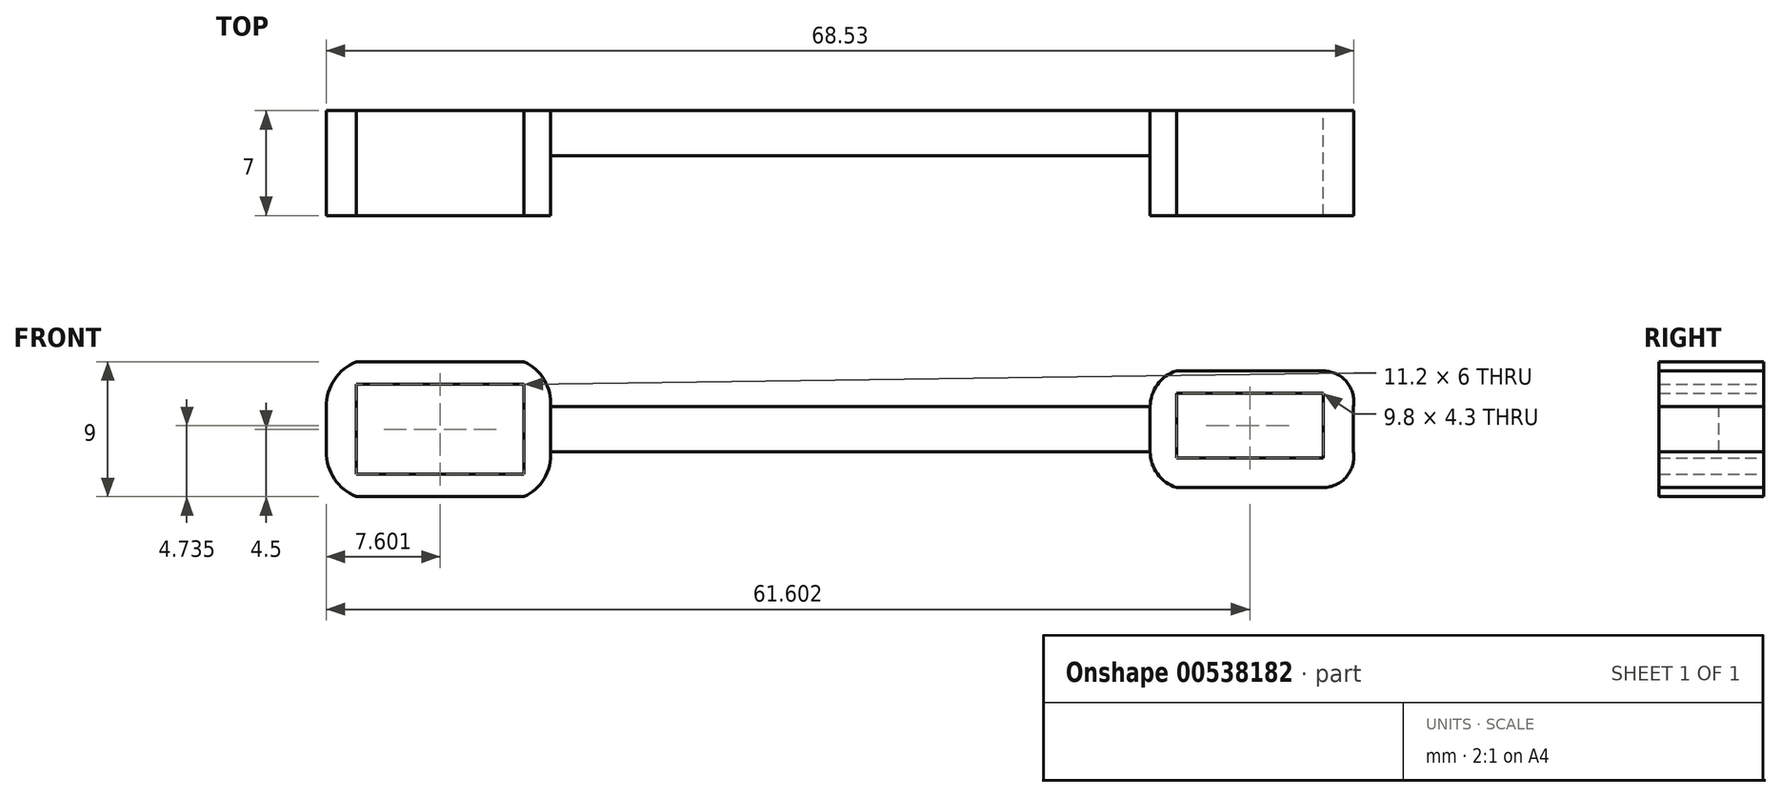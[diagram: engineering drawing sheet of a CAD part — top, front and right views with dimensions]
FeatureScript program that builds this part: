
annotation { "Feature Type Name" : "Feature", "Feature Type Description" : "" }
export const myFeature = defineFeature(function(context is Context, id is Id, definition is map)
    precondition{}
    {
        {
            var Q0;
            Q0=qCreatedBy(makeId("Front.planeOp"),FACE);
            var sketch = newSketch(context, id + "F0", { "sketchPlane" : qUnion([Q0])});
            skLineSegment(sketch, "E0.bottom", {"start": v(-27.42, 0) * mm, "end": v(12.58, 0) * mm});
            skLineSegment(sketch, "E0.top", {"start": v(-27.42, 3) * mm, "end": v(12.58, 3) * mm});
            skLineSegment(sketch, "E0.left", {"start": v(-27.42, 0) * mm, "end": v(-27.42, 3) * mm});
            skLineSegment(sketch, "E0.right", {"start": v(12.58, 0) * mm, "end": v(12.58, 3) * mm});
            skLineSegment(sketch, "E1.bottom", {"start": v(14.33, -0.42) * mm, "end": v(24.13, -0.42) * mm});
            skLineSegment(sketch, "E1.top", {"start": v(14.33, 3.88) * mm, "end": v(24.13, 3.88) * mm});
            skLineSegment(sketch, "E1.left", {"start": v(14.33, -0.42) * mm, "end": v(14.33, 3.88) * mm});
            skLineSegment(sketch, "E1.right", {"start": v(24.13, -0.42) * mm, "end": v(24.13, 3.88) * mm});
            skLineSegment(sketch, "E2.bottom", {"start": v(24.13, -2.38) * mm, "end": v(14.33, -2.38) * mm});
            skLineSegment(sketch, "E2.top", {"start": v(24.13, 5.38) * mm, "end": v(14.33, 5.38) * mm});
            skLineSegment(sketch, "E2.left", {"start": v(24.13, -2.38) * mm, "end": v(24.13, 5.38) * mm});
            skLineSegment(sketch, "E2.right", {"start": v(14.33, -2.38) * mm, "end": v(14.33, 5.38) * mm});
            skPoint(sketch, "E3", {"position": v(12.58, 1.5) * mm});
            skPoint(sketch, "E4", {"position": v(14.33, 1.5) * mm});
            skPoint(sketch, "E5", {"position": v(24.13, 1.5) * mm});
            skLineSegment(sketch, "E6.bottom", {"start": v(-40.37, -1.5) * mm, "end": v(-29.17, -1.5) * mm});
            skLineSegment(sketch, "E6.top", {"start": v(-40.37, 4.5) * mm, "end": v(-29.17, 4.5) * mm});
            skLineSegment(sketch, "E6.left", {"start": v(-40.37, -1.5) * mm, "end": v(-40.37, 4.5) * mm});
            skLineSegment(sketch, "E6.right", {"start": v(-29.17, -1.5) * mm, "end": v(-29.17, 4.5) * mm});
            skLineSegment(sketch, "E7.bottom", {"start": v(-29.17, -3) * mm, "end": v(-40.37, -3) * mm});
            skLineSegment(sketch, "E7.top", {"start": v(-29.17, 6) * mm, "end": v(-40.37, 6) * mm});
            skLineSegment(sketch, "E7.left", {"start": v(-29.17, -3) * mm, "end": v(-29.17, 6) * mm});
            skLineSegment(sketch, "E7.right", {"start": v(-40.37, -3) * mm, "end": v(-40.37, 6) * mm});
            skPoint(sketch, "E8", {"position": v(-40.37, 1.5) * mm});
            skPoint(sketch, "E9", {"position": v(-29.17, 1.5) * mm});
            skPoint(sketch, "E10", {"position": v(-27.42, 1.5) * mm});
            skLineSegment(sketch, "E11.bottom", {"start": v(25.38, 3) * mm, "end": v(26.13, 3) * mm});
            skLineSegment(sketch, "E11.top", {"start": v(25.38, 0) * mm, "end": v(26.13, 0) * mm});
            skLineSegment(sketch, "E11.left", {"start": v(25.38, 3) * mm, "end": v(25.38, 0) * mm});
            skLineSegment(sketch, "E11.right", {"start": v(26.13, 3) * mm, "end": v(26.13, 0) * mm});
            skLineSegment(sketch, "E12.bottom", {"start": v(-41.62, 3) * mm, "end": v(-42.37, 3) * mm});
            skLineSegment(sketch, "E12.top", {"start": v(-41.62, 0) * mm, "end": v(-42.37, 0) * mm});
            skLineSegment(sketch, "E12.left", {"start": v(-41.62, 3) * mm, "end": v(-41.62, 0) * mm});
            skLineSegment(sketch, "E12.right", {"start": v(-42.37, 3) * mm, "end": v(-42.37, 0) * mm});
            skArc(sketch, "E13", {"start": v(14.33, 5.38) * mm, "mid": v(13.07, 4.48) * mm, "end": v(12.58, 3) * mm});
            skArc(sketch, "E14", {"start": v(12.58, 0) * mm, "mid": v(13.07, -1.48) * mm, "end": v(14.33, -2.38) * mm});
            skArc(sketch, "E15", {"start": v(24.13, -2.38) * mm, "mid": v(25.69, -1.66) * mm, "end": v(26.13, 0) * mm});
            skArc(sketch, "E16", {"start": v(26.13, 3) * mm, "mid": v(25.69, 4.66) * mm, "end": v(24.13, 5.38) * mm});
            skArc(sketch, "E17", {"start": v(-27.42, 3) * mm, "mid": v(-27.82, 4.78) * mm, "end": v(-29.17, 6) * mm});
            skArc(sketch, "E18", {"start": v(-29.17, -3) * mm, "mid": v(-27.82, -1.78) * mm, "end": v(-27.42, 0) * mm});
            skArc(sketch, "E19", {"start": v(-40.37, 4.5) * mm, "mid": v(-41.17, 3.9) * mm, "end": v(-41.62, 3) * mm});
            skArc(sketch, "E20", {"start": v(-41.62, 0) * mm, "mid": v(-41.16, -0.9) * mm, "end": v(-40.37, -1.5) * mm});
            skArc(sketch, "E21", {"start": v(-40.37, 6) * mm, "mid": v(-41.82, 4.8) * mm, "end": v(-42.37, 3) * mm});
            skArc(sketch, "E22", {"start": v(-42.37, 0) * mm, "mid": v(-41.82, -1.8) * mm, "end": v(-40.37, -3) * mm});
            skSolve(sketch);
        }
        {
            var Q0;
            Q0=makeQuery(id+"F0.imprint","IMPRINT",FACE,{"disambiguationData":[TD([[makeQuery(id+"F0.imprint","IMPRINT",EDGE,{"derivedFrom":sQuery(id+"F0.wireOp",EDGE,"E12.bottom")}),-1.0]])]});
            var Q1;
            Q1=makeQuery(id+"F0.imprint","IMPRINT",FACE,{"disambiguationData":[TD([[makeQuery(id+"F0.imprint","IMPRINT",EDGE,{"derivedFrom":sQuery(id+"F0.wireOp",EDGE,"E12.bottom")}),1.0]])]});
            var Q2;
            Q2=makeQuery(id+"F0.imprint","IMPRINT",FACE,{"disambiguationData":[TD([[makeQuery(id+"F0.imprint","IMPRINT",EDGE,{"derivedFrom":sQuery(id+"F0.wireOp",EDGE,"E12.top")}),1.0]])]});
            var Q3;
            {var subQ0=sQuery(id+"F0.wireOp",EDGE,"E6.bottom");Q3=makeQuery(id+"F0.imprint","IMPRINT",FACE,{"disambiguationData":[TD([[makeQuery(id+"F0.imprint","IMPRINT",EDGE,{"derivedFrom":subQ0}),-1.0]])]});}
            var Q4;
            Q4=makeQuery(id+"F0.imprint","IMPRINT",FACE,{"disambiguationData":[TD([[makeQuery(id+"F0.imprint","IMPRINT",EDGE,{"derivedFrom":sQuery(id+"F0.wireOp",EDGE,"E0.left")}),1.0]])]});
            var Q5;
            {var subQ0=sQuery(id+"F0.wireOp",EDGE,"E6.top");Q5=makeQuery(id+"F0.imprint","IMPRINT",FACE,{"disambiguationData":[TD([[makeQuery(id+"F0.imprint","IMPRINT",EDGE,{"derivedFrom":subQ0}),1.0]])]});}
            var Q6;
            Q6=makeQuery(id+"F0.imprint","IMPRINT",FACE,{"disambiguationData":[TD([[makeQuery(id+"F0.imprint","IMPRINT",EDGE,{"derivedFrom":sQuery(id+"F0.wireOp",EDGE,"E12.left")}),1.0]])]});
            extrude(context, id + "F1", {"entities" : qUnion([Q0, Q1, Q2, Q3, Q4, Q5, Q6]), "depth" : 7 * mm, "offsetDistance" : 25 * mm});
        }
        {
            var Q0;
            Q0=makeQuery(id+"F0.imprint","IMPRINT",FACE,{"disambiguationData":[TD([[makeQuery(id+"F0.imprint","IMPRINT",EDGE,{"derivedFrom":sQuery(id+"F0.wireOp",EDGE,"E0.bottom")}),1.0]])]});
            extrude(context, id + "F2", {"entities" : qUnion([Q0]), "operationType" : NewBodyOperationType.ADD, "depth" : 3 * mm, "offsetDistance" : 25 * mm});
        }
        {
            var Q0;
            Q0=makeQuery(id+"F0.imprint","IMPRINT",FACE,{"disambiguationData":[TD([[makeQuery(id+"F0.imprint","IMPRINT",EDGE,{"derivedFrom":sQuery(id+"F0.wireOp",EDGE,"E0.right")}),-1.0]])]});
            var Q1;
            {var subQ0=sQuery(id+"F0.wireOp",EDGE,"E1.bottom");Q1=makeQuery(id+"F0.imprint","IMPRINT",FACE,{"disambiguationData":[TD([[makeQuery(id+"F0.imprint","IMPRINT",EDGE,{"derivedFrom":subQ0}),-1.0]])]});}
            var Q2;
            Q2=makeQuery(id+"F0.imprint","IMPRINT",FACE,{"disambiguationData":[TD([[makeQuery(id+"F0.imprint","IMPRINT",EDGE,{"derivedFrom":sQuery(id+"F0.wireOp",EDGE,"E11.bottom")}),1.0]])]});
            var Q3;
            Q3=makeQuery(id+"F0.imprint","IMPRINT",FACE,{"disambiguationData":[TD([[makeQuery(id+"F0.imprint","IMPRINT",EDGE,{"derivedFrom":sQuery(id+"F0.wireOp",EDGE,"E11.bottom")}),-1.0]])]});
            var Q4;
            {var subQ0=sQuery(id+"F0.wireOp",EDGE,"E1.top");Q4=makeQuery(id+"F0.imprint","IMPRINT",FACE,{"disambiguationData":[TD([[makeQuery(id+"F0.imprint","IMPRINT",EDGE,{"derivedFrom":subQ0}),1.0]])]});}
            extrude(context, id + "F3", {"entities" : qUnion([Q0, Q1, Q2, Q3, Q4]), "operationType" : NewBodyOperationType.ADD, "depth" : 7 * mm, "offsetDistance" : 25 * mm});
        }
    });
